# Revit family: FantiniCosmi_BIM_C32
name_source: partatom
category: Modelli generici
units: mm (PartAtom-declared; Revit-internal decimal feet)

## family parameters
Basato su piano di lavoro = No
Condiviso = No
Punto di calcolo locali = No
Può ospitare armatura = No
Quota connettore circolare = Usa diametro
Sempre verticale = Sì
Taglio con vuoti quando caricato = No
Tipo di parte = Normale

## types (1)
- Standard
    Body admissible temperature = 45 °C
    Catalog web link = https://www.fantinicosmi.it
    Color = White
    Confort regulation range = 16 ÷ 34 °C
    Descrizione = Daily programmable thermostat with mechanical clock, with batteries
    Differential = 0,25 K
    Economy regulation range = 5 ÷ 23 °C
    Part Number = Intellitherm C32
    Pollution degree = 2
    Power supply = 2 batteries AA 1,5 V
    Preset antifreeze temperature = 5 °C
    Prospetto di default = 0 mm  [stored 0 ft]
    Protection degree = IP20
    Pulse voltage = 4000 V
    Type of action = 1BU (micro disconnection)

note: [stored X ft] marks values corroborated as IEEE doubles in the binary element streams (Revit-internal decimal feet)

## geometry (parser evidence)
native form markers: Sweep x3
no freeform markers — native parametric forms only
